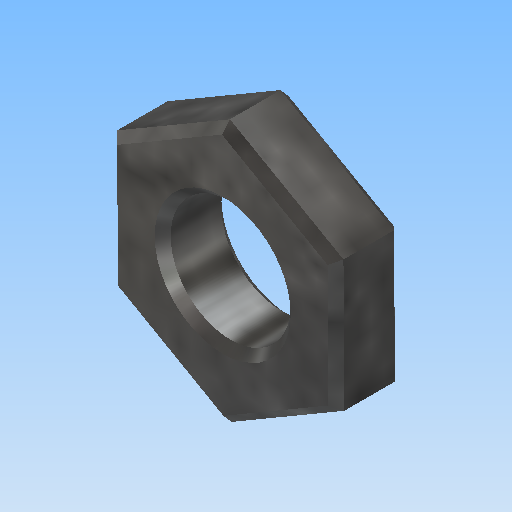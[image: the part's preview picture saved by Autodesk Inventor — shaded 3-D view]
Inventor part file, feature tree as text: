
AUTODESK INVENTOR PART (.ipt)
format: ipt  version: 2018 (Build 220112000, 112)  size: 160,256 bytes
history: native  units: mm
features: extrude x1, chamfer x1, sketch x1
ambient origin geometry x8: Origin, YZ Plane, XZ Plane, XY Plane, X Axis, Y Axis, Z Axis, Center Point
bodies: Solid1 (feature_tree)
feature tree (3):
  extrude  "Extrusion1"  Depth=5.0mm
  chamfer  "Chamfer1"  Distance=5.0mm
  sketch  "Sketch1"  dims[d0=9.02mm d1=8.5mm d2=5.0mm d3=0.0mm d4=0.6mm d5=2.0mm d6=45.0deg]
